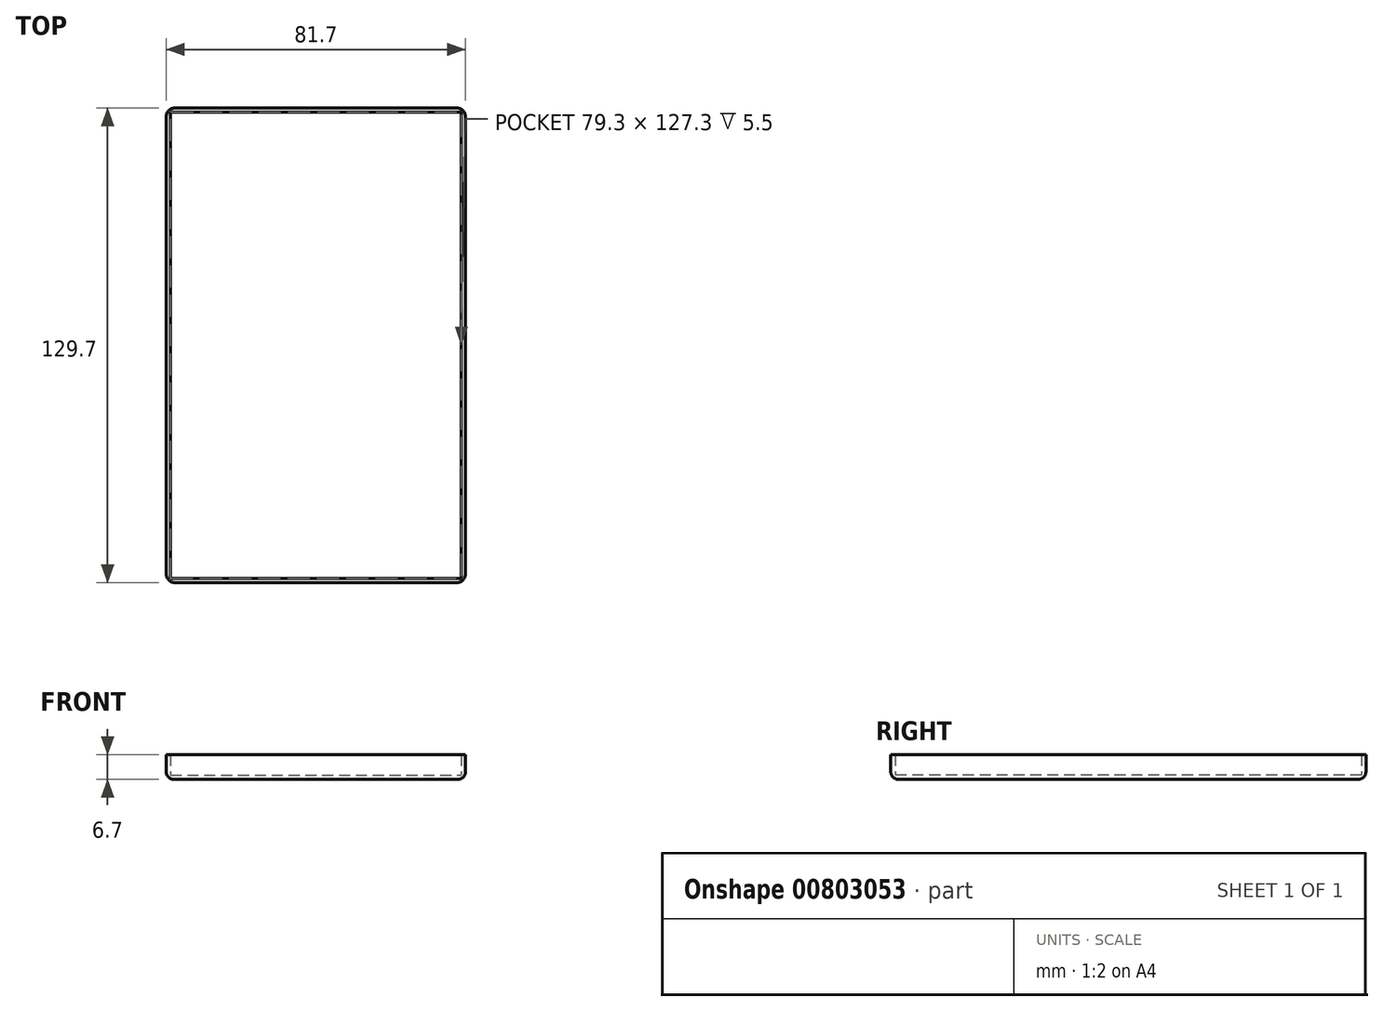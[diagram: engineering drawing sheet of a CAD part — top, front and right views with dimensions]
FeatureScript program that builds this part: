
annotation { "Feature Type Name" : "Feature", "Feature Type Description" : "" }
export const myFeature = defineFeature(function(context is Context, id is Id, definition is map)
    precondition{}
    {
        {
            var Q0;
            Q0=qCreatedBy(makeId("Top.planeOp"),FACE);
            var sketch = newSketch(context, id + "F0", { "sketchPlane" : qUnion([Q0])});
            skLineSegment(sketch, "E0", {"start": v(-47.13, -40.23) * mm, "end": v(32.17, -40.23) * mm});
            skLineSegment(sketch, "E1", {"start": v(32.17, -40.23) * mm, "end": v(32.17, 87.07) * mm});
            skLineSegment(sketch, "E2", {"start": v(32.17, 87.07) * mm, "end": v(-47.13, 87.07) * mm});
            skLineSegment(sketch, "E3", {"start": v(-47.13, 87.07) * mm, "end": v(-47.13, -40.23) * mm});
            skLineSegment(sketch, "E4.0", {"start": v(33.37, 88.27) * mm, "end": v(-48.33, 88.27) * mm});
            skLineSegment(sketch, "E4.1", {"start": v(33.37, -41.43) * mm, "end": v(33.37, 88.27) * mm});
            skLineSegment(sketch, "E4.2", {"start": v(-48.33, -41.43) * mm, "end": v(33.37, -41.43) * mm});
            skLineSegment(sketch, "E4.3", {"start": v(-48.33, 88.27) * mm, "end": v(-48.33, -41.43) * mm});
            skSolve(sketch);
        }
        {
            var Q0;
            Q0 = qSketchRegion(id + "F0", true);
            extrude(context, id + "F1", {"entities" : qUnion([Q0]), "depth" : 5.5 * mm, "offsetDistance" : 25 * mm});
        }
        {
            var Q0;
            Q0=makeQuery(id+"F0.imprint","IMPRINT",FACE,{"disambiguationData":[TD([[makeQuery(id+"F0.imprint","IMPRINT",EDGE,{"derivedFrom":sQuery(id+"F0.wireOp",EDGE,"E0")}),1.0]])]});
            var Q1;
            Q1=makeQuery(id+"F1.opExtrude","CAP_FACE",FACE,{"disambiguationData":[OSD([sQuery(id+"F0.wireOp",EDGE,"E0"),sQuery(id+"F0.wireOp",EDGE,"E1"),sQuery(id+"F0.wireOp",EDGE,"E2"),sQuery(id+"F0.wireOp",EDGE,"E3"),sQuery(id+"F0.wireOp",EDGE,"E4.0"),sQuery(id+"F0.wireOp",EDGE,"E4.1"),sQuery(id+"F0.wireOp",EDGE,"E4.2"),sQuery(id+"F0.wireOp",EDGE,"E4.3")])],"isStart":true});
            extrude(context, id + "F2", {"entities" : qUnion([Q0, Q1]), "operationType" : NewBodyOperationType.ADD, "oppositeDirection" : true, "depth" : 1.2 * mm, "offsetDistance" : 25 * mm});
        }
        {
            var Q0;
            {var subQ0=sQuery(id+"F0.wireOp",EDGE,"E4.3");var subQ1=sQuery(id+"F0.wireOp",EDGE,"E4.0");Q0=makeQuery(id+"F2.boolean.opBoolean","MERGE",EDGE,{"derivedFrom":[makeQuery(id+"F1.opExtrude","SWEPT_EDGE",EDGE,{"disambiguationData":[OSD([subQ1,subQ0])]}),makeQuery(id+"F2.opExtrude","SWEPT_EDGE",EDGE,{"disambiguationData":[OSD([subQ1,subQ0])]})]});}
            var Q1;
            {var subQ0=sQuery(id+"F0.wireOp",EDGE,"E4.3");var subQ1=sQuery(id+"F0.wireOp",EDGE,"E4.2");Q1=makeQuery(id+"F2.boolean.opBoolean","MERGE",EDGE,{"derivedFrom":[makeQuery(id+"F1.opExtrude","SWEPT_EDGE",EDGE,{"disambiguationData":[OSD([subQ1,subQ0])]}),makeQuery(id+"F2.opExtrude","SWEPT_EDGE",EDGE,{"disambiguationData":[OSD([subQ1,subQ0])]})]});}
            var Q2;
            {var subQ0=sQuery(id+"F0.wireOp",EDGE,"E4.2");var subQ1=sQuery(id+"F0.wireOp",EDGE,"E4.1");Q2=makeQuery(id+"F2.boolean.opBoolean","MERGE",EDGE,{"derivedFrom":[makeQuery(id+"F1.opExtrude","SWEPT_EDGE",EDGE,{"disambiguationData":[OSD([subQ1,subQ0])]}),makeQuery(id+"F2.opExtrude","SWEPT_EDGE",EDGE,{"disambiguationData":[OSD([subQ1,subQ0])]})]});}
            var Q3;
            {var subQ0=sQuery(id+"F0.wireOp",EDGE,"E4.1");var subQ1=sQuery(id+"F0.wireOp",EDGE,"E4.0");Q3=makeQuery(id+"F2.boolean.opBoolean","MERGE",EDGE,{"derivedFrom":[makeQuery(id+"F1.opExtrude","SWEPT_EDGE",EDGE,{"disambiguationData":[OSD([subQ1,subQ0])]}),makeQuery(id+"F2.opExtrude","SWEPT_EDGE",EDGE,{"disambiguationData":[OSD([subQ1,subQ0])]})]});}
            fillet(context, id + "F3", {"entities" : qUnion([Q0, Q1, Q2, Q3]), "radius" : 2.5 * mm, "tangentPropagation" : true, "allowEdgeOverflow" : false});
        }
        {
            var Q0;
            {var subQ0=sQuery(id+"F0.wireOp",EDGE,"E3");var subQ1=sQuery(id+"F0.wireOp",EDGE,"E2");var subQ2=sQuery(id+"F0.wireOp",EDGE,"E1");var subQ3=sQuery(id+"F0.wireOp",EDGE,"E0");Q0=makeQuery(id+"F2.boolean.opBoolean","MERGE",FACE,{"derivedFrom":[makeQuery(id+"F2.opExtrude","CAP_FACE",FACE,{"disambiguationData":[OSD([subQ3,subQ2,subQ1,subQ0])],"isStart":false}),makeQuery(id+"F2.opExtrude","CAP_FACE",FACE,{"disambiguationData":[OSD([subQ3,subQ2,subQ1,subQ0,sQuery(id+"F0.wireOp",EDGE,"E4.0"),sQuery(id+"F0.wireOp",EDGE,"E4.1"),sQuery(id+"F0.wireOp",EDGE,"E4.2"),sQuery(id+"F0.wireOp",EDGE,"E4.3")])],"isStart":false})]});}
            fillet(context, id + "F4", {"entities" : qUnion([Q0]), "radius" : 2 * mm, "tangentPropagation" : true, "allowEdgeOverflow" : false});
        }
    });
